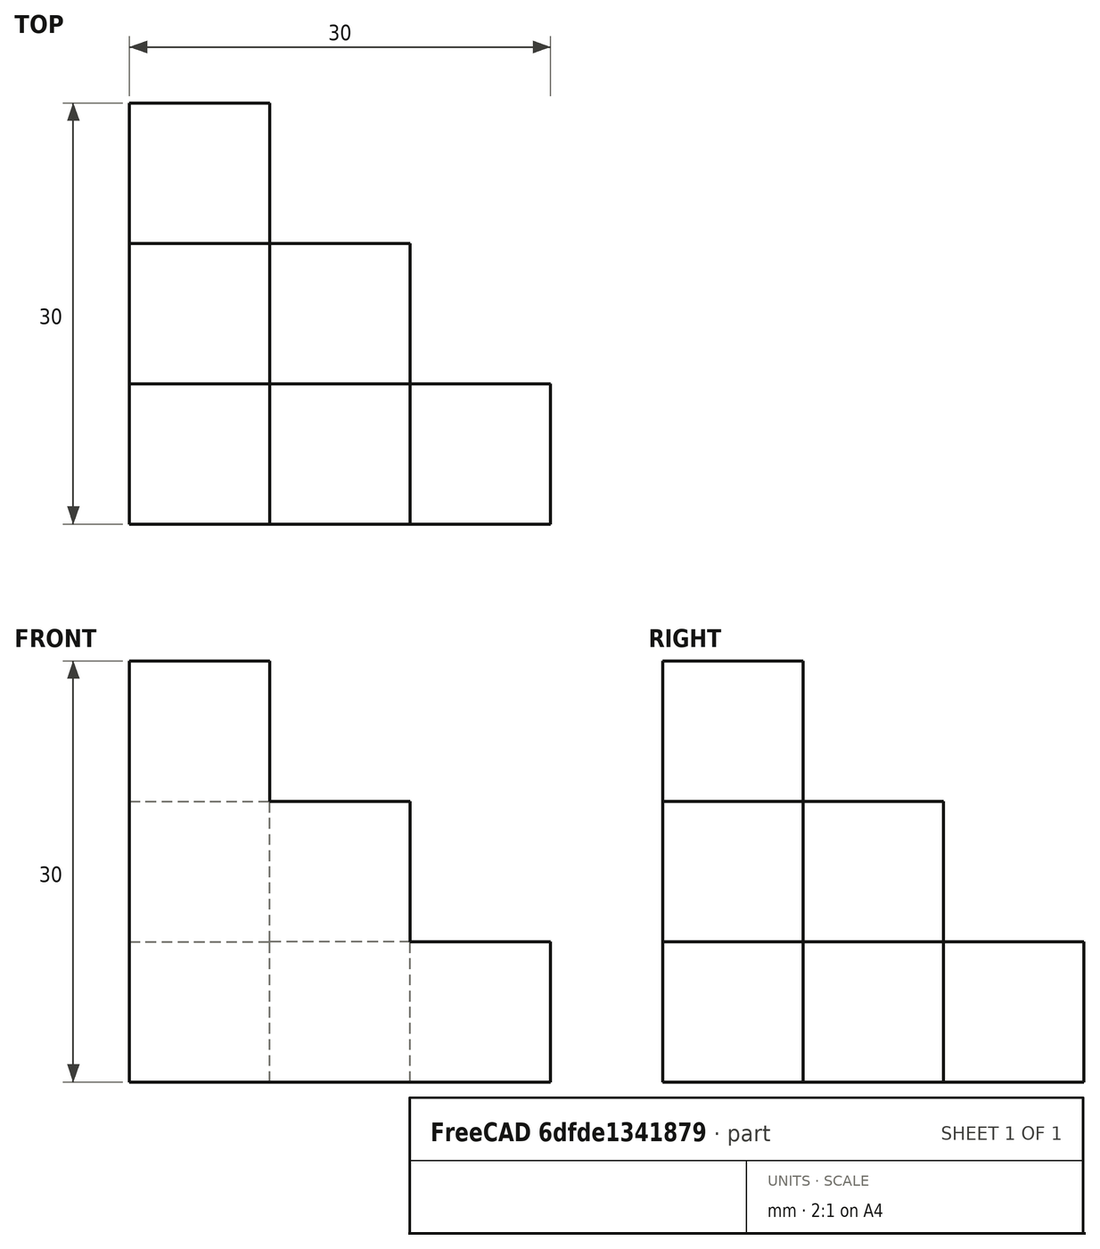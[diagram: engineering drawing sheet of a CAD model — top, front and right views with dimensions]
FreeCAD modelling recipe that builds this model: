
FCSTD DOCUMENT  (FreeCAD 1.0R39319 (Git))
Label: ojt1_t05r01_unions3nivells
License: All rights reserved
LicenseURL: https://en.wikipedia.org/wiki/All_rights_reserved
objects: Part::Box×7, Part::MultiFuse×3, Part::Fuse×3
note: 13 computed .brp shape members not serialized (recipe doc carries the construction recipe); baked Part::Feature solids carry a one-line shape summary decoded from their .brp

FEATURE [Part::Box] Box  label="Cub"
  AttacherType = Attacher::AttachEngine3D
  Height = 30
  Length = 10
  Width = 10
FEATURE [Part::Box] Box001  label="Cub001"
  AttacherType = Attacher::AttachEngine3D
  Height = 20
  Length = 10
  Placement = pos=(0,10,0) rot=(0,10,1;0rad)
  Width = 10
FEATURE [Part::Box] Box002  label="Cub002"
  AttacherType = Attacher::AttachEngine3D
  Height = 10
  Length = 10
  Placement = pos=(10,0,0) rot=(0,0,1;0rad)
  Width = 20
FEATURE [Part::Box] Box003  label="Cub003"
  AttacherType = Attacher::AttachEngine3D
  Height = 10
  Length = 10
  Placement = pos=(20,0,0) rot=(0,0,1;0rad)
  Width = 10
FEATURE [Part::Box] Box004  label="Cub004"
  AttacherType = Attacher::AttachEngine3D
  Height = 10
  Length = 10
  Placement = pos=(0,20,0) rot=(0,0,1;0rad)
  Width = 10
FEATURE [Part::Box] Box005  label="Cub005"
  AttacherType = Attacher::AttachEngine3D
  Height = 10
  Length = 10
  Width = 10
FEATURE [Part::Box] Box006  label="Cub006"
  AttacherType = Attacher::AttachEngine3D
  Height = 20
  Length = 10
  Placement = pos=(10,0,0) rot=(0,0,1;0rad)
  Width = 10
FEATURE [Part::MultiFuse] Fusion
  Refine = true
  Shapes = -> [Box,Box001,Box002,Box003,Box004,Box005,Box006]
FEATURE [Part::MultiFuse] Fusion001
  Refine = true
  Shapes = -> [Box,Box001,Box002,Box003,Box004,Box005,Box006]
FEATURE [Part::Fuse] Fusion002
  Base = -> Box
  Refine = true
  Tool = -> Box001
FEATURE [Part::Fuse] Fusion003
  Base = -> Box
  Refine = true
  Tool = -> Box001
FEATURE [Part::Fuse] Fusion004
  Base = -> Box
  Refine = true
  Tool = -> Box001
FEATURE [Part::MultiFuse] Fusion005
  Refine = true
  Shapes = -> [Fusion,Fusion001,Fusion002,Fusion003,Fusion004]
